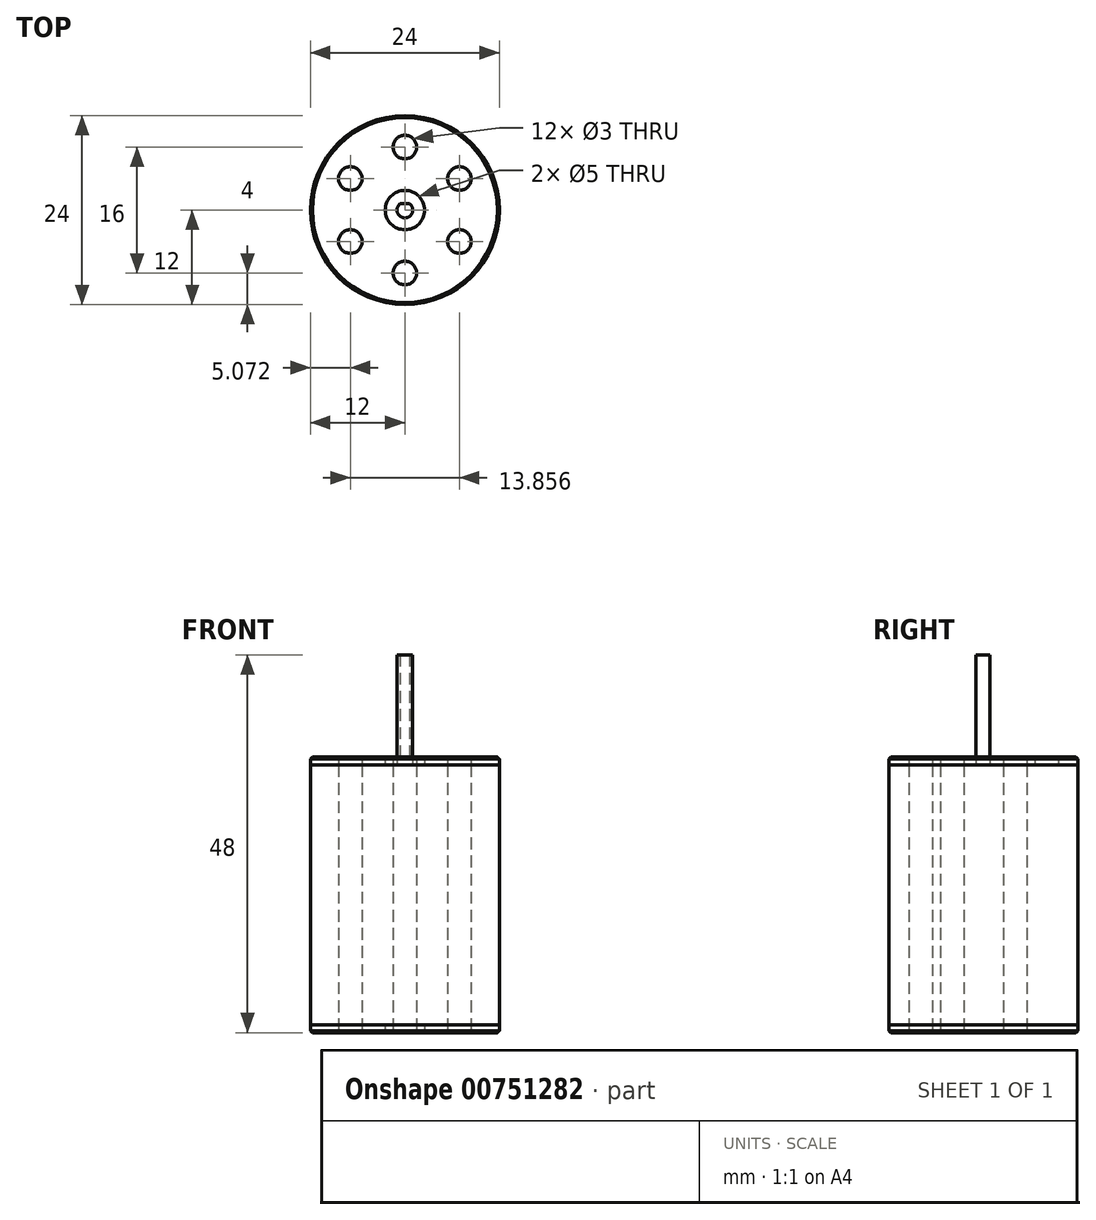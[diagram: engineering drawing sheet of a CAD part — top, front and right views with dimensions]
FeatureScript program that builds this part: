
annotation { "Feature Type Name" : "Feature", "Feature Type Description" : "" }
export const myFeature = defineFeature(function(context is Context, id is Id, definition is map)
    precondition{}
    {
        {
            assignVariable(context, id + "F0", {"name" : "bodyHeight", "anyValue" : 35});
        }
        {
            assignVariable(context, id + "F1", {"name" : "shaftHeight", "anyValue" : 14});
        }
        {
            var Q0;
            Q0=qCreatedBy(makeId("Top.planeOp"),FACE);
            var sketch = newSketch(context, id + "F2", { "sketchPlane" : qUnion([Q0])});
            skCircle(sketch, "E0", {"center": v(0, 0) * mm, "radius": 12 * mm});
            skCircle(sketch, "E1", {"center": v(0, 8) * mm, "radius": 1.5 * mm});
            skCircle(sketch, "E2", {"center": v(0, 0) * mm, "radius": 1 * mm});
            skLineSegment(sketch, "E3", {"start": v(-0.6, 0.8) * mm, "end": v(0.6, 0.8) * mm});
            skCircle(sketch, "E4", {"center": v(0, 0) * mm, "radius": 2.5 * mm});
            skCircle(sketch, "E5.MirrorC", {"center": v(0, -8) * mm, "radius": 1.5 * mm});
            skLineSegment(sketch, "E6", {"start": v(0, 0) * mm, "end": v(10.95, 10.95) * mm, "construction": true});
            skCircle(sketch, "E7", {"center": v(-6.93, 4) * mm, "radius": 1.5 * mm});
            skCircle(sketch, "E8", {"center": v(6.93, -4) * mm, "radius": 1.5 * mm});
            skLineSegment(sketch, "E9", {"start": v(6.93, -4) * mm, "end": v(-6.93, 4) * mm, "construction": true});
            skCircle(sketch, "E10.MirrorC", {"center": v(6.93, 4) * mm, "radius": 1.5 * mm});
            skCircle(sketch, "E11.MirrorC", {"center": v(-6.93, -4) * mm, "radius": 1.5 * mm});
            skSolve(sketch);
        }
        {
            var Q0;
            Q0=makeQuery(id+"F2.imprint","IMPRINT",FACE,{"disambiguationData":[TD([[makeQuery(id+"F2.imprint","IMPRINT",EDGE,{"derivedFrom":sQuery(id+"F2.wireOp",EDGE,"E7")}),1.0]])]});
            var Q1;
            Q1=makeQuery(id+"F2.imprint","IMPRINT",FACE,{"disambiguationData":[TD([[makeQuery(id+"F2.imprint","IMPRINT",EDGE,{"derivedFrom":sQuery(id+"F2.wireOp",EDGE,"E11.MirrorC")}),-1.0]])]});
            var Q2;
            Q2=makeQuery(id+"F2.imprint","IMPRINT",FACE,{"disambiguationData":[TD([[makeQuery(id+"F2.imprint","IMPRINT",EDGE,{"derivedFrom":sQuery(id+"F2.wireOp",EDGE,"E5.MirrorC")}),-1.0]])]});
            var Q3;
            Q3=makeQuery(id+"F2.imprint","IMPRINT",FACE,{"disambiguationData":[TD([[makeQuery(id+"F2.imprint","IMPRINT",EDGE,{"derivedFrom":sQuery(id+"F2.wireOp",EDGE,"E8")}),1.0]])]});
            var Q4;
            Q4=makeQuery(id+"F2.imprint","IMPRINT",FACE,{"disambiguationData":[TD([[makeQuery(id+"F2.imprint","IMPRINT",EDGE,{"derivedFrom":sQuery(id+"F2.wireOp",EDGE,"E10.MirrorC")}),-1.0]])]});
            var Q5;
            Q5=makeQuery(id+"F2.imprint","IMPRINT",FACE,{"disambiguationData":[TD([[makeQuery(id+"F2.imprint","IMPRINT",EDGE,{"derivedFrom":sQuery(id+"F2.wireOp",EDGE,"E1")}),1.0]])]});
            var Q6;
            Q6=makeQuery(id+"F2.imprint","IMPRINT",FACE,{"disambiguationData":[TD([[makeQuery(id+"F2.imprint","IMPRINT",EDGE,{"derivedFrom":sQuery(id+"F2.wireOp",EDGE,"E0")}),1.0]])]});
            extrude(context, id + "F3", {"entities" : qUnion([Q0, Q1, Q2, Q3, Q4, Q5, Q6]), "depth" : 1 * mm, "offsetDistance" : 25 * mm});
        }
        {
            var Q0;
            Q0=makeQuery(id+"F2.imprint","IMPRINT",FACE,{"disambiguationData":[TD([[makeQuery(id+"F2.imprint","IMPRINT",EDGE,{"derivedFrom":sQuery(id+"F2.wireOp",EDGE,"E11.MirrorC")}),-1.0]])]});
            var Q1;
            Q1=makeQuery(id+"F2.imprint","IMPRINT",FACE,{"disambiguationData":[TD([[makeQuery(id+"F2.imprint","IMPRINT",EDGE,{"derivedFrom":sQuery(id+"F2.wireOp",EDGE,"E5.MirrorC")}),-1.0]])]});
            var Q2;
            Q2=makeQuery(id+"F2.imprint","IMPRINT",FACE,{"disambiguationData":[TD([[makeQuery(id+"F2.imprint","IMPRINT",EDGE,{"derivedFrom":sQuery(id+"F2.wireOp",EDGE,"E10.MirrorC")}),-1.0]])]});
            var Q3;
            Q3=makeQuery(id+"F2.imprint","IMPRINT",FACE,{"disambiguationData":[TD([[makeQuery(id+"F2.imprint","IMPRINT",EDGE,{"derivedFrom":sQuery(id+"F2.wireOp",EDGE,"E8")}),1.0]])]});
            var Q4;
            Q4=makeQuery(id+"F2.imprint","IMPRINT",FACE,{"disambiguationData":[TD([[makeQuery(id+"F2.imprint","IMPRINT",EDGE,{"derivedFrom":sQuery(id+"F2.wireOp",EDGE,"E0")}),1.0]])]});
            var Q5;
            Q5=makeQuery(id+"F2.imprint","IMPRINT",FACE,{"disambiguationData":[TD([[makeQuery(id+"F2.imprint","IMPRINT",EDGE,{"derivedFrom":sQuery(id+"F2.wireOp",EDGE,"E1")}),1.0]])]});
            var Q6;
            Q6=makeQuery(id+"F2.imprint","IMPRINT",FACE,{"disambiguationData":[TD([[makeQuery(id+"F2.imprint","IMPRINT",EDGE,{"derivedFrom":sQuery(id+"F2.wireOp",EDGE,"E7")}),1.0]])]});
            var Q7;
            Q7=makeQuery(id+"F2.imprint","IMPRINT",FACE,{"disambiguationData":[TD([[makeQuery(id+"F2.imprint","IMPRINT",EDGE,{"derivedFrom":sQuery(id+"F2.wireOp",EDGE,"E4")}),1.0]])]});
            var Q8;
            {var subQ0=sQuery(id+"F2.wireOp",EDGE,"E3");Q8=makeQuery(id+"F2.imprint","IMPRINT",FACE,{"disambiguationData":[TD([[makeQuery(id+"F2.imprint","IMPRINT",EDGE,{"derivedFrom":subQ0}),-1.0]])]});}
            var Q9;
            {var subQ0=sQuery(id+"F2.wireOp",EDGE,"E3");Q9=makeQuery(id+"F2.imprint","IMPRINT",FACE,{"disambiguationData":[TD([[makeQuery(id+"F2.imprint","IMPRINT",EDGE,{"derivedFrom":subQ0}),1.0]])]});}
            var Q10;
            Q10=makeQuery(id+"F3.opExtrude","CAP_FACE",FACE,{"disambiguationData":[OSD([sQuery(id+"F2.wireOp",EDGE,"E0"),sQuery(id+"F2.wireOp",EDGE,"E4")])],"isStart":false});
            extrude(context, id + "F4", {"entities" : qUnion([Q0, Q1, Q2, Q3, Q4, Q5, Q6, Q7, Q8, Q9]), "depth" : (getVariable(context, 'bodyHeight') - 1) * mm, "offsetDistance" : 25 * mm, "hasSecondDirection" : true, "secondDirectionBound" : BoundingType.UP_TO_SURFACE, "secondDirectionOppositeDirection" : false, "secondDirectionDepth" : 1 * mm, "secondDirectionBoundEntityFace" : qUnion([Q10])});
        }
        {
            var Q0;
            Q0=makeQuery(id+"F2.imprint","IMPRINT",FACE,{"disambiguationData":[TD([[makeQuery(id+"F2.imprint","IMPRINT",EDGE,{"derivedFrom":sQuery(id+"F2.wireOp",EDGE,"E0")}),1.0]])]});
            var Q1;
            Q1=makeQuery(id+"F4.opExtrude","CAP_FACE",FACE,{"disambiguationData":[OSD([sQuery(id+"F2.wireOp",EDGE,"E0")])],"isStart":false});
            var Q2;
            Q2=makeQuery(id+"F4.opExtrude","CAP_FACE",FACE,{"disambiguationData":[OSD([sQuery(id+"F2.wireOp",EDGE,"E0")])],"isStart":false});
            extrude(context, id + "F5", {"entities" : qUnion([Q0]), "endBound" : BoundingType.UP_TO_SURFACE, "depth" : 35 * mm, "endBoundEntityFace" : qUnion([Q1]), "hasOffset" : true, "offsetDistance" : 1 * mm, "offsetOppositeDirection" : true, "hasSecondDirection" : true, "secondDirectionBound" : BoundingType.UP_TO_SURFACE, "secondDirectionOppositeDirection" : false, "secondDirectionDepth" : 34 * mm, "secondDirectionBoundEntityFace" : qUnion([Q2])});
        }
        {
            var Q0;
            {var subQ0=sQuery(id+"F2.wireOp",EDGE,"E3");Q0=makeQuery(id+"F2.imprint","IMPRINT",FACE,{"disambiguationData":[TD([[makeQuery(id+"F2.imprint","IMPRINT",EDGE,{"derivedFrom":subQ0}),-1.0]])]});}
            var Q1;
            Q1=makeQuery(id+"F4.opExtrude","CAP_FACE",FACE,{"disambiguationData":[OSD([sQuery(id+"F2.wireOp",EDGE,"E0")])],"isStart":false});
            var Q2;
            Q2=makeQuery(id+"F4.opExtrude","CAP_FACE",FACE,{"disambiguationData":[OSD([sQuery(id+"F2.wireOp",EDGE,"E0")])],"isStart":false});
            extrude(context, id + "F6", {"entities" : qUnion([Q0]), "flatOperationType" : FlatOperationType.REMOVE, "endBound" : BoundingType.UP_TO_SURFACE, "depth" : 47 * mm, "endBoundEntityFace" : qUnion([Q1]), "hasOffset" : true, "offsetDistance" : (getVariable(context, 'shaftHeight')) * mm, "offsetOppositeDirection" : true, "hasSecondDirection" : true, "secondDirectionBound" : BoundingType.UP_TO_SURFACE, "secondDirectionOppositeDirection" : false, "secondDirectionDepth" : 33 * mm, "secondDirectionBoundEntityFace" : qUnion([Q2]), "domain" : OperationDomain.MODEL});
        }
        {
            var Q0;
            Q0=makeQuery(id+"F5.opExtrude","CAP_EDGE",EDGE,{"disambiguationData":[OSD([sQuery(id+"F2.wireOp",EDGE,"E0")])],"isStart":false});
            var Q1;
            Q1=makeQuery(id+"F3.opExtrude","CAP_EDGE",EDGE,{"disambiguationData":[OSD([sQuery(id+"F2.wireOp",EDGE,"E0")])],"isStart":true});
            chamfer(context, id + "F7", {"entities" : qUnion([Q0, Q1]), "width" : .25 * mm, "tangentPropagation" : true});
        }
    });
